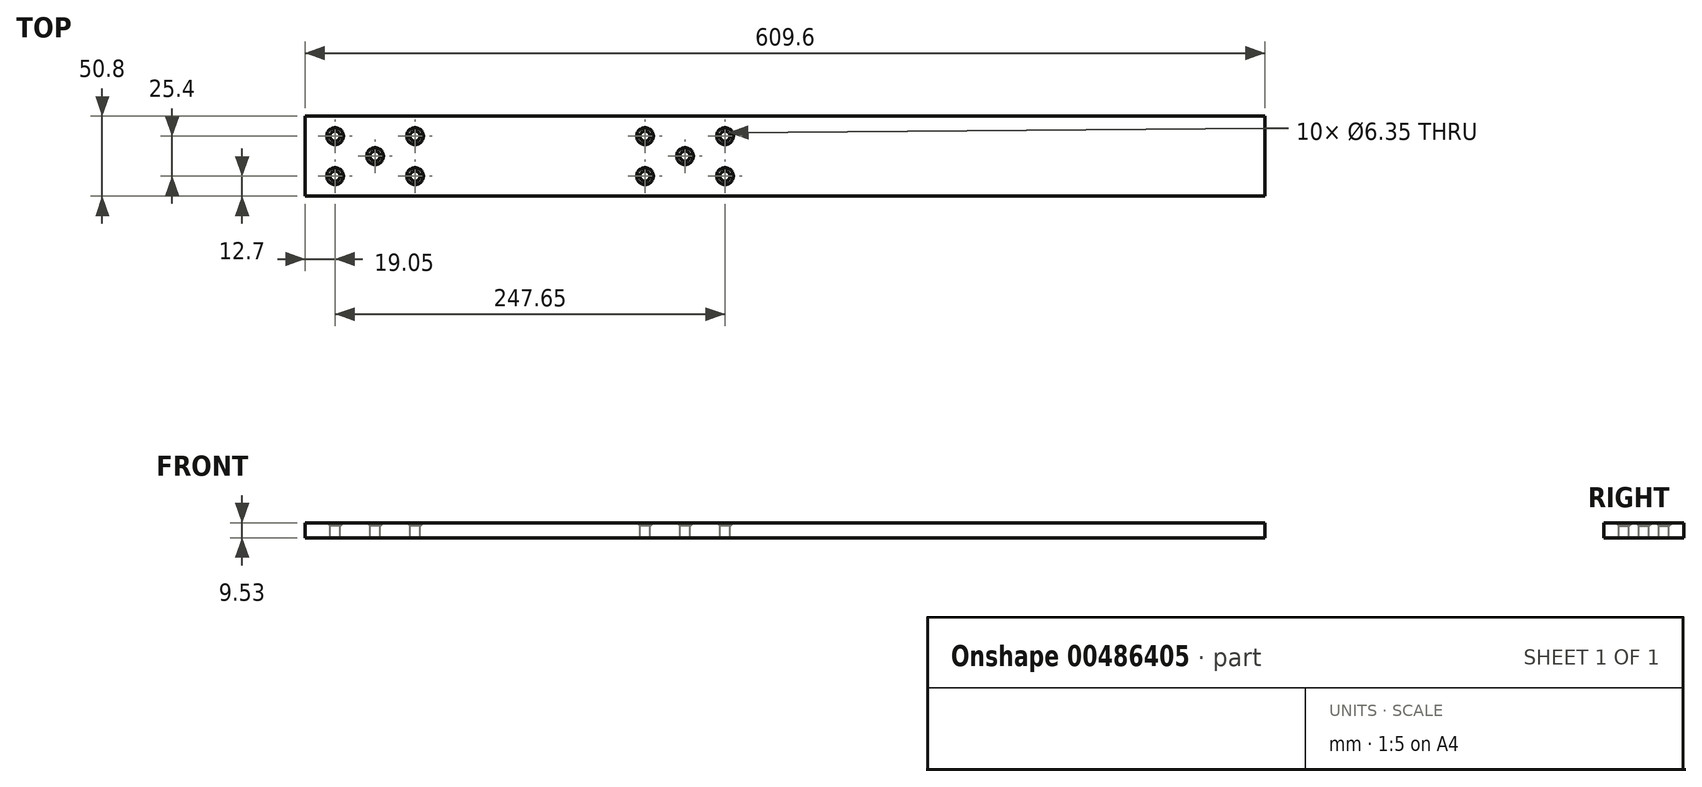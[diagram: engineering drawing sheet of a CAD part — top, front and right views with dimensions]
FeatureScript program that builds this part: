
annotation { "Feature Type Name" : "Feature", "Feature Type Description" : "" }
export const myFeature = defineFeature(function(context is Context, id is Id, definition is map)
    precondition{}
    {
        {
            var Q0;
            Q0=qCreatedBy(makeId("Top.planeOp"),FACE);
            var sketch = newSketch(context, id + "F0", { "sketchPlane" : qUnion([Q0])});
            skLineSegment(sketch, "E0.bottom", {"start": v(-304.8, 25.4) * mm, "end": v(304.8, 25.4) * mm});
            skLineSegment(sketch, "E0.top", {"start": v(-304.8, -25.4) * mm, "end": v(304.8, -25.4) * mm});
            skLineSegment(sketch, "E0.left", {"start": v(-304.8, 25.4) * mm, "end": v(-304.8, -25.4) * mm});
            skLineSegment(sketch, "E0.right", {"start": v(304.8, 25.4) * mm, "end": v(304.8, -25.4) * mm});
            skPoint(sketch, "E0.middle", {"position": v(0, 0) * mm});
            skSolve(sketch);
        }
        {
            var Q0;
            Q0 = qSketchRegion(id + "F0", true);
            extrude(context, id + "F1", {"entities" : qUnion([Q0]), "depth" : 9.52 * mm, "offsetDistance" : 25.4 * mm});
        }
        {
            var Q0;
            Q0=makeQuery(id+"F1.opExtrude","CAP_FACE",FACE,{"disambiguationData":[OSD([sQuery(id+"F0.wireOp",EDGE,"E0.bottom"),sQuery(id+"F0.wireOp",EDGE,"E0.top"),sQuery(id+"F0.wireOp",EDGE,"E0.left"),sQuery(id+"F0.wireOp",EDGE,"E0.right")])],"isStart":false});
            var sketch = newSketch(context, id + "F2", { "sketchPlane" : qUnion([Q0])});
            skLineSegment(sketch, "E1.bottom", {"start": v(-304.8, 25.4) * mm, "end": v(304.8, 25.4) * mm});
            skLineSegment(sketch, "E1.top", {"start": v(-304.8, -25.4) * mm, "end": v(304.8, -25.4) * mm});
            skLineSegment(sketch, "E1.left", {"start": v(-304.8, 25.4) * mm, "end": v(-304.8, -25.4) * mm});
            skLineSegment(sketch, "E2", {"start": v(-304.8, -12.7) * mm, "end": v(-223.65, -12.7) * mm, "construction": true});
            skLineSegment(sketch, "E3", {"start": v(-343.18, 12.7) * mm, "end": v(-304.8, 12.7) * mm, "construction": true});
            skLineSegment(sketch, "E4", {"start": v(-285.75, -25.4) * mm, "end": v(-285.75, 25.4) * mm, "construction": true});
            skLineSegment(sketch, "E5", {"start": v(-260.35, 25.4) * mm, "end": v(-260.35, -25.4) * mm, "construction": true});
            skLineSegment(sketch, "E6", {"start": v(-234.95, 25.4) * mm, "end": v(-234.95, -25.4) * mm, "construction": true});
            skCircle(sketch, "E7", {"center": v(-285.75, 12.7) * mm, "radius": 3.17 * mm});
            skCircle(sketch, "E8", {"center": v(-285.75, -12.7) * mm, "radius": 3.18 * mm});
            skCircle(sketch, "E9", {"center": v(-234.95, -12.7) * mm, "radius": 3.17 * mm});
            skPoint(sketch, "E9.centerSnap0", {"position": v(-234.95, 0) * mm});
            skCircle(sketch, "E10", {"center": v(-234.95, 12.7) * mm, "radius": 3.18 * mm});
            skCircle(sketch, "E11", {"center": v(-260.35, 0) * mm, "radius": 3.18 * mm});
            skPoint(sketch, "E12", {"position": v(-63.5, 0) * mm});
            skLineSegment(sketch, "E13", {"start": v(-108.35, -12.7) * mm, "end": v(-27.2, -12.7) * mm, "construction": true});
            skLineSegment(sketch, "E14", {"start": v(-88.9, -25.4) * mm, "end": v(-88.9, 25.4) * mm, "construction": true});
            skLineSegment(sketch, "E15", {"start": v(-63.5, 25.4) * mm, "end": v(-63.5, -25.4) * mm, "construction": true});
            skLineSegment(sketch, "E16", {"start": v(-38.1, 12.7) * mm, "end": v(-38.1, -25.4) * mm, "construction": true});
            skCircle(sketch, "E17", {"center": v(-88.9, 12.7) * mm, "radius": 3.17 * mm});
            skCircle(sketch, "E18", {"center": v(-88.9, -12.7) * mm, "radius": 3.18 * mm});
            skCircle(sketch, "E19", {"center": v(-38.1, -12.7) * mm, "radius": 3.17 * mm});
            skPoint(sketch, "E19.centerSnap0", {"position": v(-38.1, -6.35) * mm});
            skCircle(sketch, "E20", {"center": v(-38.1, 12.7) * mm, "radius": 3.18 * mm});
            skCircle(sketch, "E21", {"center": v(-63.5, 0) * mm, "radius": 3.18 * mm});
            skSolve(sketch);
        }
        {
            var Q0;
            Q0=sQuery(id+"F2.wireOp",VERTEX,"E8.center");
            var Q1;
            Q1=sQuery(id+"F2.wireOp",VERTEX,"E7.center");
            var Q2;
            Q2=sQuery(id+"F2.wireOp",VERTEX,"E11.center");
            var Q3;
            Q3=sQuery(id+"F2.wireOp",VERTEX,"E9.center");
            var Q4;
            Q4=sQuery(id+"F2.wireOp",VERTEX,"E10.center");
            var Q5;
            Q5=makeQuery(id+"F1.opExtrude","SWEPT_BODY",BODY,{"disambiguationData":[OSD([sQuery(id+"F0.wireOp",EDGE,"E0.bottom"),sQuery(id+"F0.wireOp",EDGE,"E0.top"),sQuery(id+"F0.wireOp",EDGE,"E0.left"),sQuery(id+"F0.wireOp",EDGE,"E0.right")])]});
            hole(context, id + "F3", {"style" : HoleStyle.C_SINK, "endStyle" : HoleEndStyle.THROUGH, "holeDiameter" : 6.35 * mm, "cSinkDiameter" : 10.67 * mm, "cSinkAngle" : 90 * degree, "isTappedThrough" : true, "tappedDepth" : 12.7 * mm, "tapClearance" : 3, "startFromSketch" : true, "locations" : qUnion([Q0, Q1, Q2, Q3, Q4]), "scope" : qUnion([Q5])});
        }
        {
            var Q0;
            Q0=sQuery(id+"F2.wireOp",VERTEX,"E17.center");
            var Q1;
            Q1=sQuery(id+"F2.wireOp",VERTEX,"E18.center");
            var Q2;
            Q2=sQuery(id+"F2.wireOp",VERTEX,"E12");
            var Q3;
            Q3=sQuery(id+"F2.wireOp",VERTEX,"E20.center");
            var Q4;
            Q4=sQuery(id+"F2.wireOp",VERTEX,"E19.center");
            var Q5;
            Q5=makeQuery(id+"F1.opExtrude","SWEPT_BODY",BODY,{"disambiguationData":[OSD([sQuery(id+"F0.wireOp",EDGE,"E0.bottom"),sQuery(id+"F0.wireOp",EDGE,"E0.top"),sQuery(id+"F0.wireOp",EDGE,"E0.left"),sQuery(id+"F0.wireOp",EDGE,"E0.right")])]});
            hole(context, id + "F4", {"style" : HoleStyle.C_SINK, "endStyle" : HoleEndStyle.THROUGH, "holeDiameter" : 6.35 * mm, "cSinkDiameter" : 10.67 * mm, "cSinkAngle" : 90 * degree, "isTappedThrough" : true, "tappedDepth" : 12.7 * mm, "tapClearance" : 3, "startFromSketch" : true, "locations" : qUnion([Q0, Q1, Q2, Q3, Q4]), "scope" : qUnion([Q5])});
        }
    });
